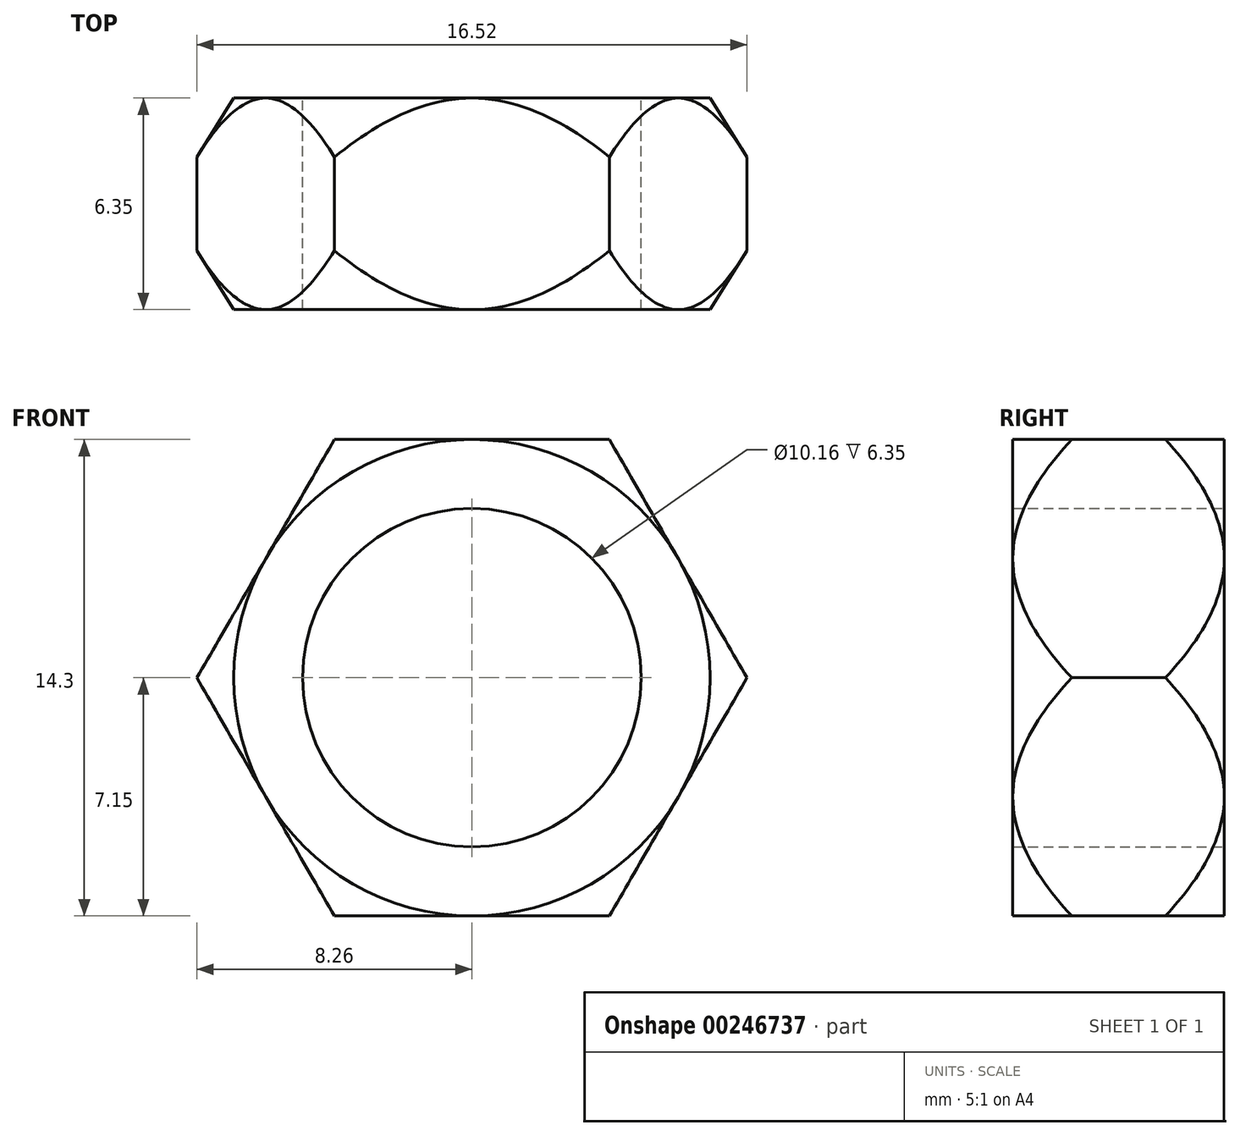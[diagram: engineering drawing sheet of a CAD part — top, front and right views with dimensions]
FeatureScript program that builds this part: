
annotation { "Feature Type Name" : "Feature", "Feature Type Description" : "" }
export const myFeature = defineFeature(function(context is Context, id is Id, definition is map)
    precondition{}
    {
        {
            var Q0;
            Q0=qCreatedBy(makeId("Front.planeOp"),FACE);
            var sketch = newSketch(context, id + "F0", { "sketchPlane" : qUnion([Q0])});
            skCircle(sketch, "E0.cCircle", {"center": v(0, 0) * mm, "radius": 8.26 * mm, "construction": true});
            skLineSegment(sketch, "E0.0", {"start": v(-8.26, 0) * mm, "end": v(-4.13, 7.15) * mm});
            skLineSegment(sketch, "E0.1", {"start": v(-4.13, 7.15) * mm, "end": v(4.13, 7.15) * mm});
            skLineSegment(sketch, "E0.2", {"start": v(4.13, 7.15) * mm, "end": v(8.26, 0) * mm});
            skLineSegment(sketch, "E0.3", {"start": v(8.26, 0) * mm, "end": v(4.13, -7.15) * mm});
            skLineSegment(sketch, "E0.4", {"start": v(4.13, -7.15) * mm, "end": v(-4.13, -7.15) * mm});
            skLineSegment(sketch, "E0.5", {"start": v(-4.13, -7.15) * mm, "end": v(-8.26, 0) * mm});
            skCircle(sketch, "E1", {"center": v(0, 0) * mm, "radius": 5.08 * mm});
            skSolve(sketch);
        }
        {
            var Q0;
            Q0 = qSketchRegion(id + "F0", true);
            extrude(context, id + "F1", {"entities" : qUnion([Q0]), "depth" : 6.35 * mm});
        }
        {
            var Q0;
            Q0=makeQuery(id+"F1.opExtrude","CAP_FACE",FACE,{"disambiguationData":[OSD([sQuery(id+"F0.wireOp",EDGE,"E0.0"),sQuery(id+"F0.wireOp",EDGE,"E0.1"),sQuery(id+"F0.wireOp",EDGE,"E0.2"),sQuery(id+"F0.wireOp",EDGE,"E0.3"),sQuery(id+"F0.wireOp",EDGE,"E0.4"),sQuery(id+"F0.wireOp",EDGE,"E0.5"),sQuery(id+"F0.wireOp",EDGE,"E1")])],"isStart":false});
            var sketch = newSketch(context, id + "F2", { "sketchPlane" : qUnion([Q0])});
            skCircle(sketch, "E2", {"center": v(0, 0) * mm, "radius": 7.15 * mm});
            skCircle(sketch, "E3", {"center": v(0, 0) * mm, "radius": 15.6 * mm});
            skSolve(sketch);
        }
        {
            var Q0;
            Q0 = qSketchRegion(id + "F2", true);
            extrude(context, id + "F3", {"entities" : qUnion([Q0]), "operationType" : NewBodyOperationType.REMOVE, "oppositeDirection" : true, "depth" : 25.4 * mm, "hasDraft" : true, "draftAngle" : 32 * degree, "draftPullDirection" : true});
        }
        {
            var Q0;
            Q0=makeQuery(id+"F1.opExtrude","CAP_FACE",FACE,{"disambiguationData":[OSD([sQuery(id+"F0.wireOp",EDGE,"E0.0"),sQuery(id+"F0.wireOp",EDGE,"E0.1"),sQuery(id+"F0.wireOp",EDGE,"E0.2"),sQuery(id+"F0.wireOp",EDGE,"E0.3"),sQuery(id+"F0.wireOp",EDGE,"E0.4"),sQuery(id+"F0.wireOp",EDGE,"E0.5"),sQuery(id+"F0.wireOp",EDGE,"E1")])],"isStart":true});
            var sketch = newSketch(context, id + "F4", { "sketchPlane" : qUnion([Q0])});
            skCircle(sketch, "E4", {"center": v(0, 0) * mm, "radius": 7.15 * mm});
            skCircle(sketch, "E5", {"center": v(0, 0) * mm, "radius": 19.03 * mm});
            skSolve(sketch);
        }
        {
            var Q0;
            Q0 = qSketchRegion(id + "F4", true);
            extrude(context, id + "F5", {"entities" : qUnion([Q0]), "operationType" : NewBodyOperationType.REMOVE, "oppositeDirection" : true, "depth" : 25.4 * mm, "hasDraft" : true, "draftAngle" : 32 * degree, "draftPullDirection" : true});
        }
    });
